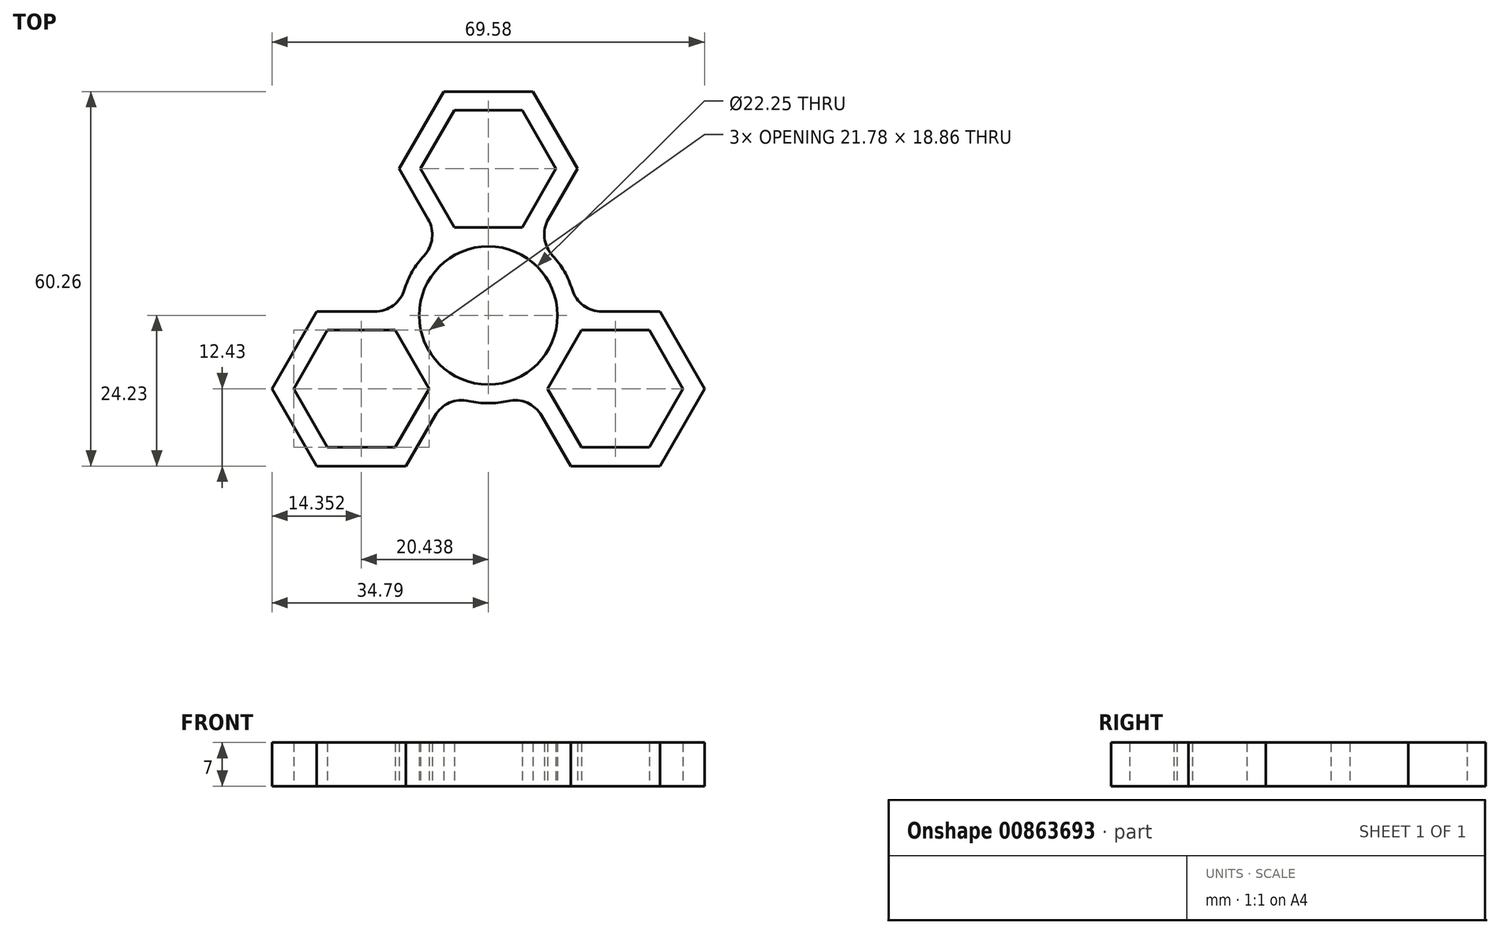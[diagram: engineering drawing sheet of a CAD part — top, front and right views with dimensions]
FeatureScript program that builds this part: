
annotation { "Feature Type Name" : "Feature", "Feature Type Description" : "" }
export const myFeature = defineFeature(function(context is Context, id is Id, definition is map)
    precondition{}
    {
        {
            var Q0;
            Q0=qCreatedBy(makeId("Top.planeOp"),FACE);
            var sketch = newSketch(context, id + "F0", { "sketchPlane" : qUnion([Q0])});
            skCircle(sketch, "E0", {"center": v(0, 0) * mm, "radius": 11.12 * mm});
            skLineSegment(sketch, "E1.0", {"start": v(-5.44, 33.03) * mm, "end": v(5.44, 33.03) * mm});
            skLineSegment(sketch, "E1.1", {"start": v(5.44, 33.03) * mm, "end": v(10.89, 23.6) * mm});
            skLineSegment(sketch, "E1.2", {"start": v(10.89, 23.6) * mm, "end": v(5.44, 14.17) * mm});
            skLineSegment(sketch, "E1.3", {"start": v(5.44, 14.17) * mm, "end": v(-5.44, 14.17) * mm});
            skLineSegment(sketch, "E1.4", {"start": v(-5.44, 14.17) * mm, "end": v(-10.89, 23.6) * mm});
            skLineSegment(sketch, "E1.5", {"start": v(-10.89, 23.6) * mm, "end": v(-5.44, 33.03) * mm});
            skPoint(sketch, "E1.0.midPoint", {"position": v(0, 33.03) * mm});
            skLineSegment(sketch, "E2.0", {"start": v(-7.18, 36.03) * mm, "end": v(7.18, 36.03) * mm});
            skLineSegment(sketch, "E2.1", {"start": v(7.18, 36.03) * mm, "end": v(14.35, 23.6) * mm});
            skLineSegment(sketch, "E2.2", {"start": v(14.35, 23.6) * mm, "end": v(9.68, 15.51) * mm});
            skLineSegment(sketch, "E2.4", {"start": v(-9.68, 15.51) * mm, "end": v(-14.35, 23.6) * mm});
            skLineSegment(sketch, "E2.5", {"start": v(-14.35, 23.6) * mm, "end": v(-7.18, 36.03) * mm});
            skPoint(sketch, "E2.0.midPoint", {"position": v(0, 36.03) * mm});
            skLineSegment(sketch, "E3.1.0", {"start": v(-25.88, -2.37) * mm, "end": v(-15, -2.37) * mm});
            skLineSegment(sketch, "E3.1.1", {"start": v(-25.88, -21.23) * mm, "end": v(-31.33, -11.8) * mm});
            skLineSegment(sketch, "E3.1.2", {"start": v(-15, -2.37) * mm, "end": v(-9.55, -11.8) * mm});
            skPoint(sketch, "E3.1.3", {"position": v(-28.6, -16.51) * mm});
            skLineSegment(sketch, "E3.1.4", {"start": v(-34.8, -11.8) * mm, "end": v(-27.61, 0.63) * mm});
            skLineSegment(sketch, "E3.1.5", {"start": v(-27.61, 0.63) * mm, "end": v(-18.28, 0.63) * mm});
            skLineSegment(sketch, "E3.1.6", {"start": v(-9.55, -11.8) * mm, "end": v(-15, -21.23) * mm});
            skLineSegment(sketch, "E3.1.7", {"start": v(-27.61, -24.23) * mm, "end": v(-34.8, -11.8) * mm});
            skPoint(sketch, "E3.1.8", {"position": v(-31.2, -18.01) * mm});
            skLineSegment(sketch, "E3.1.9", {"start": v(-8.6, -16.14) * mm, "end": v(-13.26, -24.23) * mm});
            skLineSegment(sketch, "E3.1.10", {"start": v(-31.33, -11.8) * mm, "end": v(-25.88, -2.37) * mm});
            skLineSegment(sketch, "E3.1.11", {"start": v(-13.26, -24.23) * mm, "end": v(-27.61, -24.23) * mm});
            skLineSegment(sketch, "E3.1.12", {"start": v(-15, -21.23) * mm, "end": v(-25.88, -21.23) * mm});
            skLineSegment(sketch, "E3.2.0", {"start": v(15, -21.23) * mm, "end": v(9.55, -11.8) * mm});
            skLineSegment(sketch, "E3.2.1", {"start": v(31.33, -11.8) * mm, "end": v(25.88, -21.23) * mm});
            skPoint(sketch, "E3.2.3", {"position": v(28.6, -16.52) * mm});
            skLineSegment(sketch, "E3.2.4", {"start": v(27.61, -24.23) * mm, "end": v(13.26, -24.23) * mm});
            skLineSegment(sketch, "E3.2.5", {"start": v(13.26, -24.23) * mm, "end": v(8.6, -16.14) * mm});
            skLineSegment(sketch, "E3.2.6", {"start": v(15, -2.37) * mm, "end": v(25.88, -2.37) * mm});
            skLineSegment(sketch, "E3.2.7", {"start": v(34.8, -11.8) * mm, "end": v(27.61, -24.23) * mm});
            skPoint(sketch, "E3.2.8", {"position": v(31.2, -18.02) * mm});
            skLineSegment(sketch, "E3.2.9", {"start": v(18.28, 0.63) * mm, "end": v(27.61, 0.63) * mm});
            skLineSegment(sketch, "E3.2.10", {"start": v(25.88, -21.23) * mm, "end": v(15, -21.23) * mm});
            skLineSegment(sketch, "E3.2.11", {"start": v(27.61, 0.63) * mm, "end": v(34.8, -11.8) * mm});
            skLineSegment(sketch, "E3.2.12", {"start": v(25.88, -2.37) * mm, "end": v(31.33, -11.8) * mm});
            skArc(sketch, "E4.0", {"start": v(-10.35, 9.61) * mm, "mid": v(-12.23, 7.06) * mm, "end": v(-13.5, 4.16) * mm});
            skArc(sketch, "E5.trimOffspring", {"start": v(-3.15, -13.77) * mm, "mid": v(0, -14.12) * mm, "end": v(3.15, -13.77) * mm});
            skArc(sketch, "E6.trimOffspring", {"start": v(13.5, 4.16) * mm, "mid": v(12.23, 7.06) * mm, "end": v(10.35, 9.61) * mm});
            skPoint(sketch, "E7.newPointA", {"position": v(-7.18, 11.17) * mm});
            skArc(sketch, "E7.filletArc", {"start": v(-10.35, 9.61) * mm, "mid": v(-9.05, 12.45) * mm, "end": v(-9.68, 15.51) * mm});
            skPoint(sketch, "E8.newPointA", {"position": v(-13.26, 0.63) * mm});
            skArc(sketch, "E8.filletArc", {"start": v(-18.28, 0.63) * mm, "mid": v(-15.3, 1.6) * mm, "end": v(-13.5, 4.16) * mm});
            skPoint(sketch, "E9.newPointA", {"position": v(-6.09, -11.8) * mm});
            skArc(sketch, "E9.filletArc", {"start": v(-3.15, -13.77) * mm, "mid": v(-6.26, -14.06) * mm, "end": v(-8.6, -16.14) * mm});
            skPoint(sketch, "E10.newPointB", {"position": v(6.09, -11.8) * mm});
            skArc(sketch, "E10.filletArc", {"start": v(8.6, -16.14) * mm, "mid": v(6.26, -14.06) * mm, "end": v(3.15, -13.77) * mm});
            skPoint(sketch, "E11.newPointA", {"position": v(13.26, 0.63) * mm});
            skArc(sketch, "E11.filletArc", {"start": v(13.5, 4.16) * mm, "mid": v(15.3, 1.6) * mm, "end": v(18.28, 0.63) * mm});
            skPoint(sketch, "E12.newPointB", {"position": v(7.18, 11.17) * mm});
            skArc(sketch, "E12.filletArc", {"start": v(9.68, 15.51) * mm, "mid": v(9.05, 12.45) * mm, "end": v(10.35, 9.61) * mm});
            skLineSegment(sketch, "E13", {"start": v(15, -2.37) * mm, "end": v(9.55, -11.8) * mm});
            skSolve(sketch);
        }
        {
            var Q0;
            Q0 = qSketchRegion(id + "F0", true);
            extrude(context, id + "F1", {"entities" : qUnion([Q0]), "depth" : 7 * mm, "offsetDistance" : 25 * mm});
        }
    });
